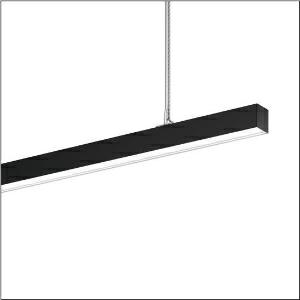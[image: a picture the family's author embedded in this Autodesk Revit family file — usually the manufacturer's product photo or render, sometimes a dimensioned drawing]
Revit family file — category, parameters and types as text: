
# Revit family: silica_r__21_51mx30dc39bb_25b6
name_source: partatom
category: Lighting Fixtures
units: mm (PartAtom-declared; Revit-internal decimal feet)

## family parameters
Cut with Voids When Loaded = No
Host = Face
Light Source = No
Part Type = Normal
Room Calculation Point = No
Round Connector Dimension = Use Diameter
Shared = No

## types (1)
- --- (1 x LED, 10520 lm, 68.3 W, 3000K)
    Apparent Load = 68 VA
    CIE Flux Codes = 47 79 96 57 100
    Color Rendering = 80
    Color Temperature = 3000K
    Default Elevation = 1800 mm
    Description = Silica® 21, office luminaire, primary optical cover: cover, of PMMA, opal, light emission: direct/indirect distribution, primary light characteristic: symmetric, installation type: suspended mounting, LED, rated luminous flux: 10.520lm, luminous efficacy: 154lm/W, light colour: 830, colour temperature: 3000K, with terminal, 3+2-pole, max. 2.5mm², mains connection: 220..240V, AC, 50/60Hz, rated input power: 68.3W, luminaire housing, of aluminium, jet black (RAL 9005), length: 3.004mm, width: 53mm, height: 53mm, protection rating (complete): IP20, insulation class (complete): insulation class I (protective earthing), certification: CE, permissible operating ambient temperature: 0..+35°C, standard: EN 50419, packaging unit: 1 piece
    Height = 53 mm
    Lamp = 1 x LED
    Lamp Light Flux = 10520 lm
    Lamp Power = 68.3 W
    Lamp count = 1
    Length = 3004 mm
    Luminous efficacy = 154 lm/W
    Manufacturer = Siteco
    ModVariant = No
    Model = 51MX30DC39BB
    Mounting Place = Ceiling
    Mounting Type = Pendant
    Number of Poles = 1
    OnlyDefault = Yes
    Power Factor = 1
    Product Name = Silica® 21
    Product group = office luminaire | ceiling pendant
    ProductGroupID = 902
    Protection Class = Protection class I
    Protection Degree = IP 20
    RLX_Detail_Level = 1
    RLX_Emergency_Light_Flux = 0 lm
    RLX_Emergency_Type = 0
    RLX_Emergency_Type_DB = No
    RlxData = <blob elided: 26069 chars, md5=29956f2b>
    Socket = socket
    Standby Power = 0 W
    System Light Flux = 10520 lm
    System Power = 68 W
    Type Comments = factory setting: luminous flux: 100 % | dim-lin: 254 | 233 mA
    Type Image = l_1313646.jpg
    URL = http://relux.com
    VarID = @adj_065423
    Voltage = 0 V
    Weight = 0.00 kg
    Width = 53 mm

## geometry (parser evidence)
native form markers: Blend x4, Sweep x13
no freeform markers — native parametric forms only
